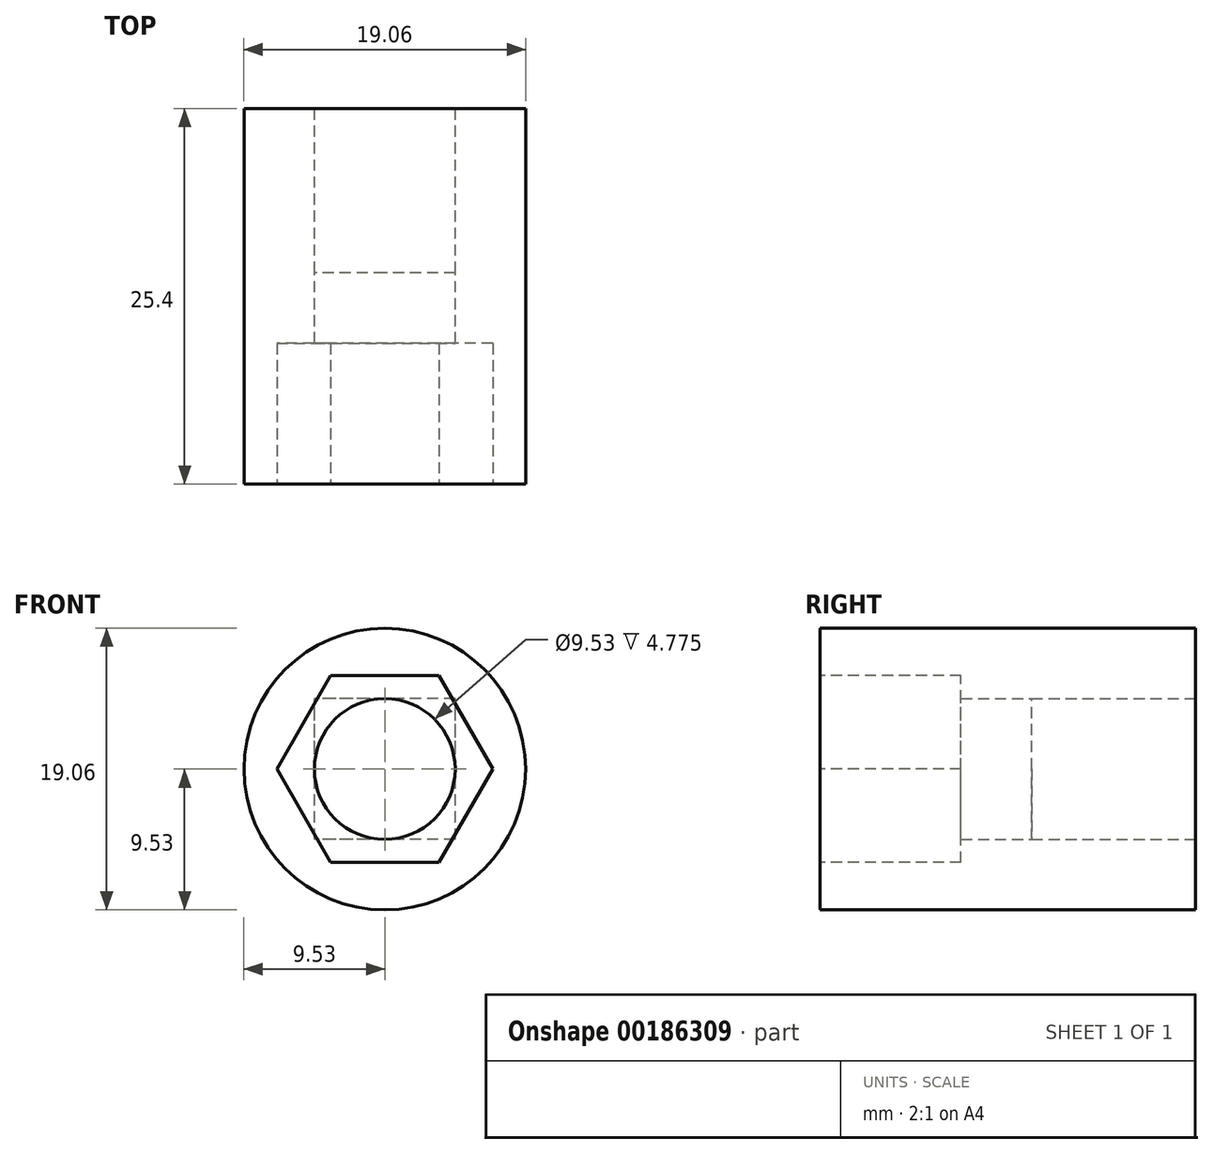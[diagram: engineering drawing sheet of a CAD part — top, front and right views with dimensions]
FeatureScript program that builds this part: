
annotation { "Feature Type Name" : "Feature", "Feature Type Description" : "" }
export const myFeature = defineFeature(function(context is Context, id is Id, definition is map)
    precondition{}
    {
        {
            var Q0;
            Q0=qCreatedBy(makeId("Front.planeOp"),FACE);
            var sketch = newSketch(context, id + "F0", { "sketchPlane" : qUnion([Q0])});
            skCircle(sketch, "E0", {"center": v(0, 0) * mm, "radius": 9.53 * mm});
            skSolve(sketch);
        }
        {
            var Q0;
            Q0 = qSketchRegion(id + "F0", true);
            extrude(context, id + "F1", {"entities" : qUnion([Q0]), "depth" : 25.4 * mm});
        }
        {
            var Q0;
            Q0=qCreatedBy(makeId("Front.planeOp"),FACE);
            var sketch = newSketch(context, id + "F2", { "sketchPlane" : qUnion([Q0])});
            skLineSegment(sketch, "E1.bottom", {"start": v(4.76, -4.76) * mm, "end": v(-4.76, -4.76) * mm});
            skLineSegment(sketch, "E1.top", {"start": v(4.76, 4.76) * mm, "end": v(-4.76, 4.76) * mm});
            skLineSegment(sketch, "E1.left", {"start": v(4.76, -4.76) * mm, "end": v(4.76, 4.76) * mm});
            skLineSegment(sketch, "E1.right", {"start": v(-4.76, -4.76) * mm, "end": v(-4.76, 4.76) * mm});
            skPoint(sketch, "E1.middle", {"position": v(0, 0) * mm});
            skCircle(sketch, "E2", {"center": v(0, 0) * mm, "radius": 4.76 * mm});
            skSolve(sketch);
        }
        {
            var Q0;
            {var subQ0=sQuery(id+"F2.wireOp",EDGE,"E2");var subQ1=makeQuery(id+"F2.imprint","INTERSECT",VERTEX,{"derivedFrom":[sQuery(id+"F2.wireOp",EDGE,"E1.top"),subQ0]});Q0=makeQuery(id+"F2.imprint","IMPRINT",FACE,{"disambiguationData":[TD([[makeQuery(id+"F2.imprint","IMPRINT",EDGE,{"disambiguationData":[TD([[subQ1,1.0]])],"derivedFrom":subQ0}),1.0]])]});}
            var Q1;
            Q1=sQuery(id+"F2.wireOp",EDGE,"E2");
            extrude(context, id + "F3", {"entities" : qUnion([Q0]), "operationType" : NewBodyOperationType.REMOVE, "surfaceEntities" : qUnion([Q1]), "endBound" : BoundingType.THROUGH_ALL, "depth" : 25.4 * mm});
        }
        {
            var Q0;
            Q0 = qSketchRegion(id + "F2", true);
            extrude(context, id + "F4", {"entities" : qUnion([Q0]), "operationType" : NewBodyOperationType.REMOVE, "depth" : 11.1 * mm});
        }
        {
            var Q0;
            Q0=makeQuery(id+"F1.opExtrude","CAP_FACE",FACE,{"disambiguationData":[OSD([sQuery(id+"F0.wireOp",EDGE,"E0")])],"isStart":false});
            var sketch = newSketch(context, id + "F5", { "sketchPlane" : qUnion([Q0])});
            skCircle(sketch, "E3.cCircle", {"center": v(0, 0) * mm, "radius": 7.3 * mm, "construction": true});
            skLineSegment(sketch, "E3.0", {"start": v(-7.3, 0) * mm, "end": v(-3.65, 6.32) * mm});
            skLineSegment(sketch, "E3.1", {"start": v(-3.65, 6.32) * mm, "end": v(3.65, 6.32) * mm});
            skLineSegment(sketch, "E3.2", {"start": v(3.65, 6.32) * mm, "end": v(7.3, 0) * mm});
            skLineSegment(sketch, "E3.3", {"start": v(7.3, 0) * mm, "end": v(3.65, -6.32) * mm});
            skLineSegment(sketch, "E3.4", {"start": v(3.65, -6.32) * mm, "end": v(-3.65, -6.32) * mm});
            skLineSegment(sketch, "E3.5", {"start": v(-3.65, -6.32) * mm, "end": v(-7.3, 0) * mm});
            skSolve(sketch);
        }
        {
            var Q0;
            Q0 = qSketchRegion(id + "F5", true);
            extrude(context, id + "F6", {"entities" : qUnion([Q0]), "operationType" : NewBodyOperationType.REMOVE, "oppositeDirection" : true, "depth" : 9.52 * mm});
        }
    });
